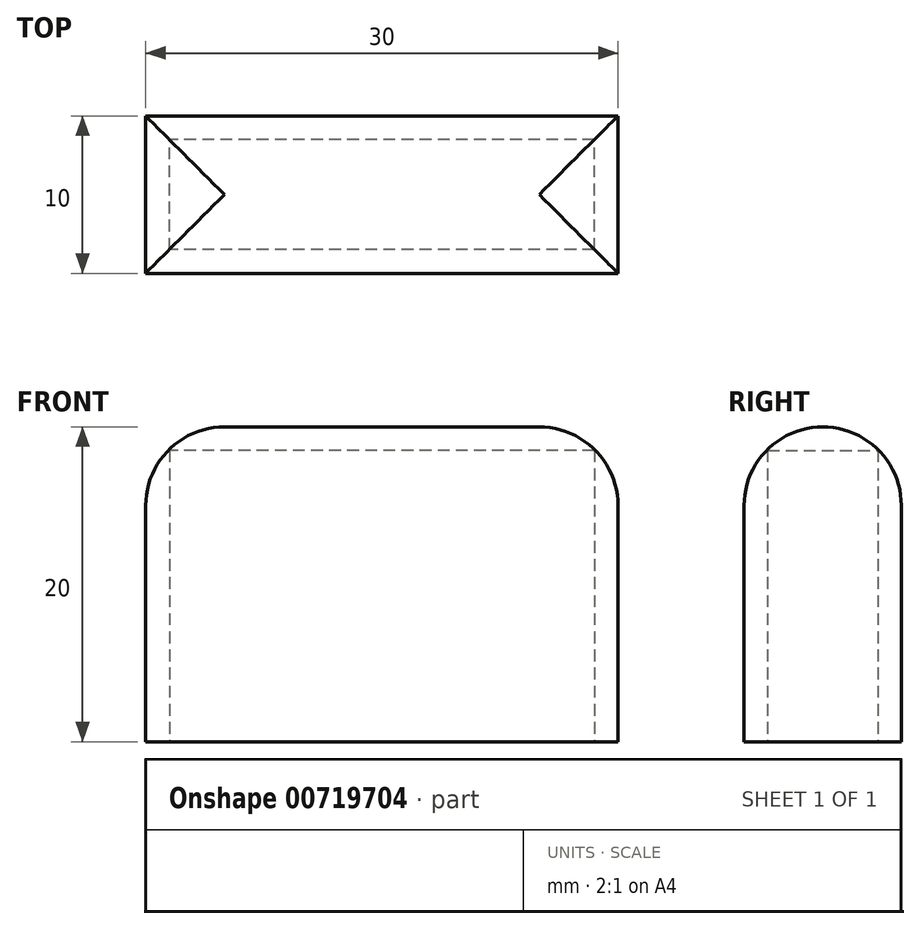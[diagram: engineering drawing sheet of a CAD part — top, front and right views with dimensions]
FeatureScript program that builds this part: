
annotation { "Feature Type Name" : "Feature", "Feature Type Description" : "" }
export const myFeature = defineFeature(function(context is Context, id is Id, definition is map)
    precondition{}
    {
        {
            var Q0;
            Q0=qCreatedBy(makeId("Top.planeOp"),FACE);
            var sketch = newSketch(context, id + "F0", { "sketchPlane" : qUnion([Q0])});
            skLineSegment(sketch, "E0.bottom", {"start": v(15, -5) * mm, "end": v(-15, -5) * mm});
            skLineSegment(sketch, "E0.top", {"start": v(15, 5) * mm, "end": v(-15, 5) * mm});
            skLineSegment(sketch, "E0.left", {"start": v(15, -5) * mm, "end": v(15, 5) * mm});
            skLineSegment(sketch, "E0.right", {"start": v(-15, -5) * mm, "end": v(-15, 5) * mm});
            skPoint(sketch, "E0.middle", {"position": v(0, 0) * mm});
            skSolve(sketch);
        }
        {
            var Q0;
            Q0=makeQuery(id+"F0.imprint","IMPRINT",FACE,{"disambiguationData":[TD([[makeQuery(id+"F0.imprint","IMPRINT",EDGE,{"derivedFrom":sQuery(id+"F0.wireOp",EDGE,"E0.bottom")}),-1.0]])]});
            extrude(context, id + "F1", {"entities" : qUnion([Q0]), "depth" : 20 * mm, "offsetDistance" : 25 * mm});
        }
        {
            var Q0;
            Q0=makeQuery(id+"F1.opExtrude","CAP_FACE",FACE,{"disambiguationData":[OSD([sQuery(id+"F0.wireOp",EDGE,"E0.bottom"),sQuery(id+"F0.wireOp",EDGE,"E0.top"),sQuery(id+"F0.wireOp",EDGE,"E0.left"),sQuery(id+"F0.wireOp",EDGE,"E0.right")])],"isStart":true});
            shell(context, id + "F2", {"entities" : qUnion([Q0]), "thickness" : 1.5 * mm});
        }
        {
            var Q0;
            Q0=makeQuery(id+"F1.opExtrude","CAP_EDGE",EDGE,{"disambiguationData":[OSD([sQuery(id+"F0.wireOp",EDGE,"E0.right")])],"isStart":false});
            var Q1;
            Q1=makeQuery(id+"F1.opExtrude","CAP_EDGE",EDGE,{"disambiguationData":[OSD([sQuery(id+"F0.wireOp",EDGE,"E0.bottom")])],"isStart":false});
            var Q2;
            Q2=makeQuery(id+"F1.opExtrude","CAP_EDGE",EDGE,{"disambiguationData":[OSD([sQuery(id+"F0.wireOp",EDGE,"E0.top")])],"isStart":false});
            var Q3;
            Q3=makeQuery(id+"F1.opExtrude","CAP_EDGE",EDGE,{"disambiguationData":[OSD([sQuery(id+"F0.wireOp",EDGE,"E0.left")])],"isStart":false});
            fillet(context, id + "F3", {"entities" : qUnion([Q0, Q1, Q2, Q3]), "radius" : 5 * mm, "tangentPropagation" : true, "allowEdgeOverflow" : false});
        }
    });
